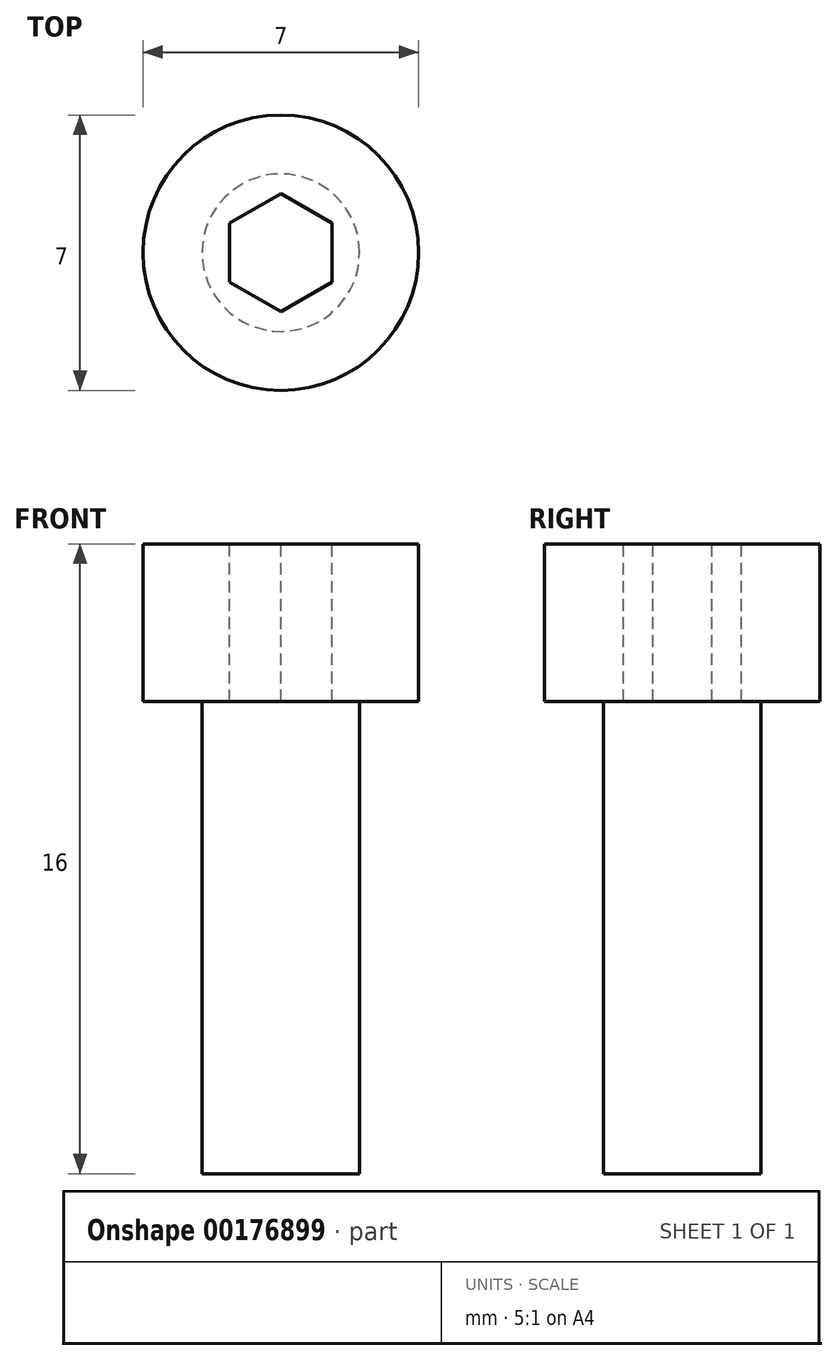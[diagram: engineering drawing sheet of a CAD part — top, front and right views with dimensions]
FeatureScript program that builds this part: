
annotation { "Feature Type Name" : "Feature", "Feature Type Description" : "" }
export const myFeature = defineFeature(function(context is Context, id is Id, definition is map)
    precondition{}
    {
        {
            var Q0;
            Q0=qCreatedBy(makeId("Top.planeOp"),FACE);
            var sketch = newSketch(context, id + "F0", { "sketchPlane" : qUnion([Q0])});
            skCircle(sketch, "E0", {"center": v(0, 0) * mm, "radius": 3.5 * mm});
            skCircle(sketch, "E1", {"center": v(0, 0) * mm, "radius": 2 * mm});
            skSolve(sketch);
        }
        {
            var Q0;
            Q0=makeQuery(id+"F0.imprint","IMPRINT",FACE,{"disambiguationData":[TD([[makeQuery(id+"F0.imprint","IMPRINT",EDGE,{"derivedFrom":sQuery(id+"F0.wireOp",EDGE,"E0")}),1.0]])]});
            var Q1;
            Q1=makeQuery(id+"F0.imprint","IMPRINT",FACE,{"disambiguationData":[TD([[makeQuery(id+"F0.imprint","IMPRINT",EDGE,{"derivedFrom":sQuery(id+"F0.wireOp",EDGE,"E1")}),1.0]])]});
            extrude(context, id + "F1", {"entities" : qUnion([Q0, Q1]), "depth" : 4 * mm});
        }
        {
            var Q0;
            Q0=makeQuery(id+"F0.imprint","IMPRINT",FACE,{"disambiguationData":[TD([[makeQuery(id+"F0.imprint","IMPRINT",EDGE,{"derivedFrom":sQuery(id+"F0.wireOp",EDGE,"E1")}),1.0]])]});
            extrude(context, id + "F2", {"entities" : qUnion([Q0]), "operationType" : NewBodyOperationType.ADD, "oppositeDirection" : true, "depth" : 12 * mm});
        }
        {
            var Q0;
            Q0=makeQuery(id+"F1.opExtrude","CAP_FACE",FACE,{"disambiguationData":[OSD([sQuery(id+"F0.wireOp",EDGE,"E0")])],"isStart":false});
            var sketch = newSketch(context, id + "F3", { "sketchPlane" : qUnion([Q0])});
            skCircle(sketch, "E2.cCircle", {"center": v(0, 0) * mm, "radius": 1.5 * mm, "construction": true});
            skLineSegment(sketch, "E2.0", {"start": v(0, -1.5) * mm, "end": v(-1.3, -0.75) * mm});
            skLineSegment(sketch, "E2.1", {"start": v(-1.3, -0.75) * mm, "end": v(-1.3, 0.75) * mm});
            skLineSegment(sketch, "E2.2", {"start": v(-1.3, 0.75) * mm, "end": v(0, 1.5) * mm});
            skLineSegment(sketch, "E2.3", {"start": v(0, 1.5) * mm, "end": v(1.3, 0.75) * mm});
            skLineSegment(sketch, "E2.4", {"start": v(1.3, 0.75) * mm, "end": v(1.3, -0.75) * mm});
            skLineSegment(sketch, "E2.5", {"start": v(1.3, -0.75) * mm, "end": v(0, -1.5) * mm});
            skSolve(sketch);
        }
        {
            var Q0;
            Q0=makeQuery(id+"F3.imprint","IMPRINT",FACE,{"disambiguationData":[TD([[makeQuery(id+"F3.imprint","IMPRINT",EDGE,{"derivedFrom":sQuery(id+"F3.wireOp",EDGE,"E2.0")}),-1.0]])]});
            var Q1;
            Q1=makeQuery(id+"F1.opExtrude","CAP_FACE",FACE,{"disambiguationData":[OSD([sQuery(id+"F0.wireOp",EDGE,"E0")])],"isStart":true});
            extrude(context, id + "F4", {"entities" : qUnion([Q0]), "operationType" : NewBodyOperationType.REMOVE, "endBound" : BoundingType.UP_TO_SURFACE, "oppositeDirection" : true, "endBoundEntityFace" : qUnion([Q1]), "depth" : 25 * mm});
        }
    });
